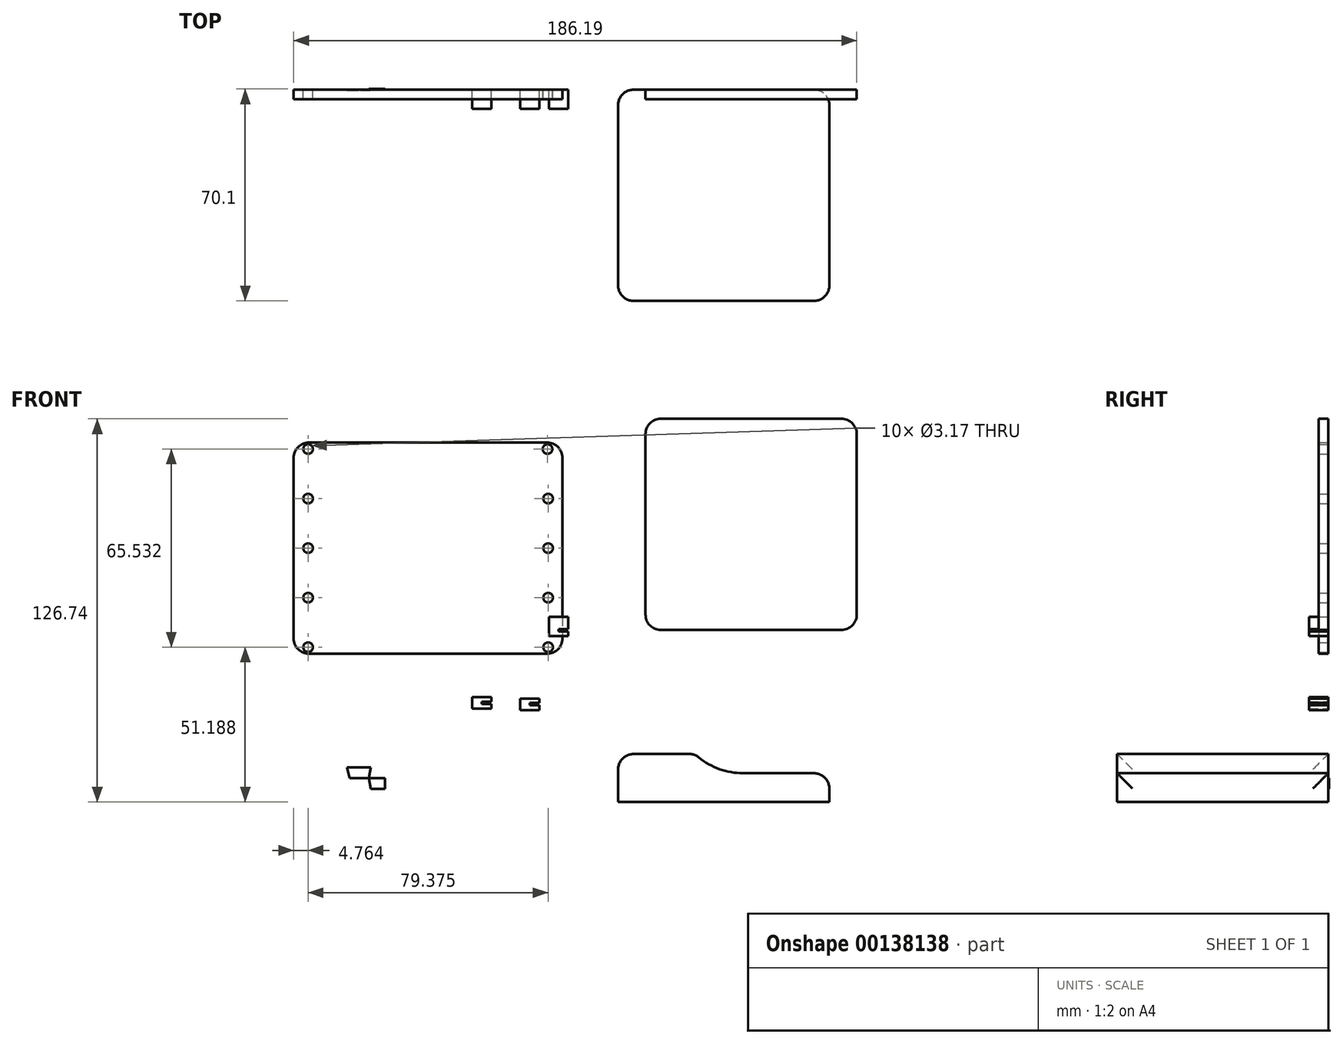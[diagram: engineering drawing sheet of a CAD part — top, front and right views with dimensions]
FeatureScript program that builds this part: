
annotation { "Feature Type Name" : "Feature", "Feature Type Description" : "" }
export const myFeature = defineFeature(function(context is Context, id is Id, definition is map)
    precondition{}
    {
        {
            var Q0;
            Q0=qCreatedBy(makeId("Front.planeOp"),FACE);
            var sketch = newSketch(context, id + "F0", { "sketchPlane" : qUnion([Q0])});
            skLineSegment(sketch, "E0.bottom", {"start": v(-88.22, 61.99) * mm, "end": v(0.68, 61.99) * mm});
            skLineSegment(sketch, "E0.top", {"start": v(-88.22, -7.86) * mm, "end": v(0.68, -7.86) * mm});
            skLineSegment(sketch, "E0.left", {"start": v(-88.22, 61.99) * mm, "end": v(-88.22, -7.86) * mm});
            skLineSegment(sketch, "E0.right", {"start": v(0.68, 61.99) * mm, "end": v(0.68, -7.86) * mm});
            skLineSegment(sketch, "E1", {"start": v(-78.7, 61.99) * mm, "end": v(-78.7, -7.86) * mm});
            skLineSegment(sketch, "E2", {"start": v(-8.84, 61.99) * mm, "end": v(-8.84, -7.86) * mm});
            skPoint(sketch, "E3.end.orphan", {"position": v(-78.7, 41.86) * mm});
            skPoint(sketch, "E4.end.orphan", {"position": v(-8.84, 36.83) * mm});
            skPoint(sketch, "E4.start.orphan", {"position": v(0.68, 41.86) * mm});
            skCircle(sketch, "E5", {"center": v(-83.46, 27.06) * mm, "radius": 1.59 * mm});
            skPoint(sketch, "E6.orphan", {"position": v(-88.22, 27.06) * mm});
            skPoint(sketch, "E7.trimOffspring.end.orphan", {"position": v(-78.7, 27.06) * mm});
            skCircle(sketch, "E8", {"center": v(-83.46, -5.7) * mm, "radius": 1.59 * mm});
            skPoint(sketch, "E9.end.orphan", {"position": v(-83.46, -7.29) * mm});
            skCircle(sketch, "E10", {"center": v(-83.46, 10.68) * mm, "radius": 1.59 * mm});
            skPoint(sketch, "E11.end.orphan", {"position": v(-83.46, -4.11) * mm});
            skPoint(sketch, "E11.start.orphan", {"position": v(-83.46, 9.1) * mm});
            skPoint(sketch, "E12.end.orphan", {"position": v(-83.46, 12.27) * mm});
            skPoint(sketch, "E12.start.orphan", {"position": v(-83.46, 25.48) * mm});
            skCircle(sketch, "E13", {"center": v(-83.46, 59.83) * mm, "radius": 1.59 * mm});
            skCircle(sketch, "E14", {"center": v(-83.46, 43.45) * mm, "radius": 1.59 * mm});
            skPoint(sketch, "E15.orphan", {"position": v(-83.46, 61.42) * mm});
            skPoint(sketch, "E16.end.orphan", {"position": v(-83.46, 58.24) * mm});
            skPoint(sketch, "E17.orphan", {"position": v(-83.46, 45.03) * mm});
            skPoint(sketch, "E18.end.orphan", {"position": v(-83.46, 41.86) * mm});
            skPoint(sketch, "E18.start.orphan", {"position": v(-83.46, 28.65) * mm});
            skCircle(sketch, "E19", {"center": v(-4.08, 27.06) * mm, "radius": 1.59 * mm});
            skCircle(sketch, "E20", {"center": v(-4.08, 10.68) * mm, "radius": 1.59 * mm});
            skCircle(sketch, "E21", {"center": v(-4.08, -5.7) * mm, "radius": 1.59 * mm});
            skPoint(sketch, "E22.end.orphan", {"position": v(-4.08, -7.29) * mm});
            skPoint(sketch, "E23.end.orphan", {"position": v(-4.08, -4.11) * mm});
            skPoint(sketch, "E23.start.orphan", {"position": v(-4.08, 9.1) * mm});
            skPoint(sketch, "E24.start.orphan", {"position": v(-4.08, 12.27) * mm});
            skPoint(sketch, "E25.orphan", {"position": v(-8.84, 27.06) * mm});
            skPoint(sketch, "E26.orphan", {"position": v(0.68, 27.06) * mm});
            skCircle(sketch, "E27", {"center": v(-4.08, 43.45) * mm, "radius": 1.59 * mm});
            skCircle(sketch, "E28", {"center": v(-4.28, 59.83) * mm, "radius": 1.59 * mm});
            skPoint(sketch, "E29.orphan", {"position": v(-4.28, 61.42) * mm});
            skPoint(sketch, "E30.end.orphan", {"position": v(-4.28, 58.24) * mm});
            skPoint(sketch, "E31.orphan", {"position": v(-4.08, 45.03) * mm});
            skPoint(sketch, "E32.end.orphan", {"position": v(-4.08, 41.86) * mm});
            skPoint(sketch, "E32.start.orphan", {"position": v(-4.08, 28.65) * mm});
            skSolve(sketch);
        }
        {
            var Q0;
            Q0 = qSketchRegion(id + "F0", true);
            extrude(context, id + "F1", {"entities" : qUnion([Q0]), "depth" : 3.17 * mm});
        }
        {
            var Q0;
            Q0=makeQuery(id+"F1.opExtrude","SWEPT_EDGE",EDGE,{"disambiguationData":[OSD([sQuery(id+"F0.wireOp",EDGE,"E0.top"),sQuery(id+"F0.wireOp",EDGE,"E0.left")])]});
            var Q1;
            Q1=makeQuery(id+"F1.opExtrude","SWEPT_EDGE",EDGE,{"disambiguationData":[OSD([sQuery(id+"F0.wireOp",EDGE,"E0.top"),sQuery(id+"F0.wireOp",EDGE,"E0.right")])]});
            var Q2;
            Q2=makeQuery(id+"F1.opExtrude","SWEPT_EDGE",EDGE,{"disambiguationData":[OSD([sQuery(id+"F0.wireOp",EDGE,"E0.bottom"),sQuery(id+"F0.wireOp",EDGE,"E0.right")])]});
            var Q3;
            Q3=makeQuery(id+"F1.opExtrude","SWEPT_EDGE",EDGE,{"disambiguationData":[OSD([sQuery(id+"F0.wireOp",EDGE,"E0.bottom"),sQuery(id+"F0.wireOp",EDGE,"E0.left")])]});
            fillet(context, id + "F2", {"entities" : qUnion([Q0, Q1, Q2, Q3]), "radius" : 5.08 * mm, "tangentPropagation" : true, "allowEdgeOverflow" : false});
        }
        {
            var Q0;
            Q0=qCreatedBy(makeId("Front.planeOp"),FACE);
            var sketch = newSketch(context, id + "F3", { "sketchPlane" : qUnion([Q0])});
            skLineSegment(sketch, "E33.bottom", {"start": v(28.12, 69.85) * mm, "end": v(97.97, 69.85) * mm});
            skLineSegment(sketch, "E33.top", {"start": v(28.12, 0) * mm, "end": v(97.97, 0) * mm});
            skLineSegment(sketch, "E33.left", {"start": v(28.12, 69.85) * mm, "end": v(28.12, 0) * mm});
            skLineSegment(sketch, "E33.right", {"start": v(97.97, 69.85) * mm, "end": v(97.97, 0) * mm});
            skSolve(sketch);
        }
        {
            var Q0;
            Q0 = qSketchRegion(id + "F3", true);
            extrude(context, id + "F4", {"entities" : qUnion([Q0]), "depth" : 3.17 * mm});
        }
        {
            var Q0;
            Q0=makeQuery(id+"F4.opExtrude","SWEPT_EDGE",EDGE,{"disambiguationData":[OSD([sQuery(id+"F3.wireOp",EDGE,"E33.bottom"),sQuery(id+"F3.wireOp",EDGE,"E33.left")])]});
            var Q1;
            Q1=makeQuery(id+"F4.opExtrude","SWEPT_EDGE",EDGE,{"disambiguationData":[OSD([sQuery(id+"F3.wireOp",EDGE,"E33.top"),sQuery(id+"F3.wireOp",EDGE,"E33.left")])]});
            var Q2;
            Q2=makeQuery(id+"F4.opExtrude","SWEPT_EDGE",EDGE,{"disambiguationData":[OSD([sQuery(id+"F3.wireOp",EDGE,"E33.top"),sQuery(id+"F3.wireOp",EDGE,"E33.right")])]});
            var Q3;
            Q3=makeQuery(id+"F4.opExtrude","SWEPT_EDGE",EDGE,{"disambiguationData":[OSD([sQuery(id+"F3.wireOp",EDGE,"E33.bottom"),sQuery(id+"F3.wireOp",EDGE,"E33.right")])]});
            fillet(context, id + "F5", {"entities" : qUnion([Q0, Q1, Q2, Q3]), "radius" : 5.08 * mm, "tangentPropagation" : true, "allowEdgeOverflow" : false});
        }
        {
            var Q0;
            Q0=qCreatedBy(makeId("Front.planeOp"),FACE);
            var sketch = newSketch(context, id + "F6", { "sketchPlane" : qUnion([Q0])});
            skLineSegment(sketch, "E34", {"start": v(19.06, -56.9) * mm, "end": v(88.9, -56.9) * mm});
            skLineSegment(sketch, "E35", {"start": v(19.06, -56.9) * mm, "end": v(19.06, -41.02) * mm});
            skLineSegment(sketch, "E36", {"start": v(19.06, -41.02) * mm, "end": v(44.46, -41.02) * mm});
            skLineSegment(sketch, "E37", {"start": v(88.9, -56.9) * mm, "end": v(88.9, -47.37) * mm});
            skLineSegment(sketch, "E38", {"start": v(88.9, -47.37) * mm, "end": v(60.33, -47.37) * mm});
            skArc(sketch, "E39", {"start": v(44.46, -41.02) * mm, "mid": v(51.78, -45.72) * mm, "end": v(60.33, -47.37) * mm});
            skPoint(sketch, "E40.start.orphan", {"position": v(44.46, -47.37) * mm});
            skSolve(sketch);
        }
        {
            var Q0;
            Q0 = qSketchRegion(id + "F6", true);
            extrude(context, id + "F7", {"entities" : qUnion([Q0]), "depth" : 69.85 * mm});
        }
        {
            var Q0;
            Q0=makeQuery(id+"F7.opExtrude","SWEPT_EDGE",EDGE,{"disambiguationData":[OSD([sQuery(id+"F6.wireOp",EDGE,"E35"),sQuery(id+"F6.wireOp",EDGE,"E36")])]});
            var Q1;
            Q1=makeQuery(id+"F7.opExtrude","SWEPT_EDGE",EDGE,{"disambiguationData":[OSD([sQuery(id+"F6.wireOp",EDGE,"E36"),sQuery(id+"F6.wireOp",EDGE,"E39")])]});
            var Q2;
            Q2=makeQuery(id+"F7.opExtrude","SWEPT_EDGE",EDGE,{"disambiguationData":[OSD([sQuery(id+"F6.wireOp",EDGE,"E37"),sQuery(id+"F6.wireOp",EDGE,"E38")])]});
            var Q3;
            Q3=makeQuery(id+"F7.opExtrude","CAP_EDGE",EDGE,{"disambiguationData":[OSD([sQuery(id+"F6.wireOp",EDGE,"E37")])],"isStart":true});
            var Q4;
            Q4=makeQuery(id+"F7.opExtrude","CAP_EDGE",EDGE,{"disambiguationData":[OSD([sQuery(id+"F6.wireOp",EDGE,"E35")])],"isStart":true});
            var Q5;
            Q5=makeQuery(id+"F7.opExtrude","CAP_EDGE",EDGE,{"disambiguationData":[OSD([sQuery(id+"F6.wireOp",EDGE,"E35")])],"isStart":false});
            var Q6;
            Q6=makeQuery(id+"F7.opExtrude","CAP_EDGE",EDGE,{"disambiguationData":[OSD([sQuery(id+"F6.wireOp",EDGE,"E37")])],"isStart":false});
            fillet(context, id + "F8", {"entities" : qUnion([Q0, Q1, Q2, Q3, Q4, Q5, Q6]), "radius" : 5.08 * mm, "tangentPropagation" : true, "allowEdgeOverflow" : false});
        }
        {
            var Q0;
            Q0=qCreatedBy(makeId("Front.planeOp"),FACE);
            var sketch = newSketch(context, id + "F9", { "sketchPlane" : qUnion([Q0])});
            skLineSegment(sketch, "E41", {"start": v(-69.73, -48.95) * mm, "end": v(-63.38, -48.95) * mm});
            skLineSegment(sketch, "E42", {"start": v(-70.59, -45.4) * mm, "end": v(-62.71, -45.4) * mm});
            skLineSegment(sketch, "E43", {"start": v(-70.59, -45.4) * mm, "end": v(-69.73, -48.95) * mm});
            skLineSegment(sketch, "E44", {"start": v(-62.71, -45.4) * mm, "end": v(-63.38, -48.95) * mm});
            skPoint(sketch, "E45.start.orphan", {"position": v(-66.65, -45.4) * mm});
            skSolve(sketch);
        }
        {
            var Q0;
            Q0 = qSketchRegion(id + "F9", true);
            extrude(context, id + "F10", {"entities" : qUnion([Q0]), "depth" : 0.25 * mm});
        }
        {
            var Q0;
            Q0=qCreatedBy(makeId("Front.planeOp"),FACE);
            var sketch = newSketch(context, id + "F11", { "sketchPlane" : qUnion([Q0])});
            skLineSegment(sketch, "E46", {"start": v(-63.38, -48.94) * mm, "end": v(-58.02, -48.94) * mm});
            skLineSegment(sketch, "E47", {"start": v(-63.38, -48.94) * mm, "end": v(-62.72, -52.52) * mm});
            skLineSegment(sketch, "E48", {"start": v(-62.72, -52.52) * mm, "end": v(-58.02, -52.52) * mm});
            skLineSegment(sketch, "E49", {"start": v(-58.02, -52.52) * mm, "end": v(-58.02, -48.94) * mm});
            skPoint(sketch, "E50.end.orphan", {"position": v(-62.72, -45.38) * mm});
            skPoint(sketch, "E51.end.orphan", {"position": v(-58.02, -45.38) * mm});
            skSolve(sketch);
        }
        {
            var Q0;
            Q0 = qSketchRegion(id + "F11", true);
            extrude(context, id + "F12", {"entities" : qUnion([Q0]), "operationType" : NewBodyOperationType.ADD, "oppositeDirection" : true, "depth" : 0.25 * mm});
        }
        {
            var Q0;
            Q0=qCreatedBy(makeId("Front.planeOp"),FACE);
            var sketch = newSketch(context, id + "F13", { "sketchPlane" : qUnion([Q0])});
            skLineSegment(sketch, "E52.bottom", {"start": v(-29.15, -22.21) * mm, "end": v(-22.8, -22.21) * mm});
            skLineSegment(sketch, "E52.top", {"start": v(-29.15, -26.02) * mm, "end": v(-22.8, -26.02) * mm});
            skLineSegment(sketch, "E52.left", {"start": v(-29.15, -22.21) * mm, "end": v(-29.15, -26.02) * mm});
            skPoint(sketch, "E53.endSnap0", {"position": v(-25.97, -22.21) * mm});
            skPoint(sketch, "E54.end.orphan", {"position": v(-25.97, -26.02) * mm});
            skPoint(sketch, "E55.orphan", {"position": v(-25.97, -30.47) * mm});
            skLineSegment(sketch, "E56", {"start": v(-22.8, -22.21) * mm, "end": v(-22.8, -23.7) * mm});
            skLineSegment(sketch, "E57", {"start": v(-22.8, -23.7) * mm, "end": v(-25.97, -23.7) * mm});
            skLineSegment(sketch, "E58", {"start": v(-25.97, -23.7) * mm, "end": v(-25.97, -24.45) * mm});
            skLineSegment(sketch, "E59", {"start": v(-25.97, -24.45) * mm, "end": v(-22.8, -24.45) * mm});
            skLineSegment(sketch, "E60", {"start": v(-22.8, -24.45) * mm, "end": v(-22.8, -26.02) * mm});
            skLineSegment(sketch, "E61.bottom", {"start": v(-3.75, 4.31) * mm, "end": v(2.6, 4.31) * mm});
            skLineSegment(sketch, "E61.top", {"start": v(-3.75, -2.04) * mm, "end": v(2.6, -2.04) * mm});
            skLineSegment(sketch, "E61.left", {"start": v(-3.75, 4.31) * mm, "end": v(-3.75, -2.04) * mm});
            skPoint(sketch, "E62.endSnap0", {"position": v(-0.58, 4.31) * mm});
            skPoint(sketch, "E63.end.orphan", {"position": v(-0.58, -2.04) * mm});
            skPoint(sketch, "E64.orphan", {"position": v(-0.58, -6.48) * mm});
            skLineSegment(sketch, "E65", {"start": v(2.6, 4.31) * mm, "end": v(2.6, 0.3) * mm});
            skLineSegment(sketch, "E66", {"start": v(2.6, 0.3) * mm, "end": v(-0.58, 0.3) * mm});
            skLineSegment(sketch, "E67", {"start": v(-0.58, 0.3) * mm, "end": v(-0.58, -0.46) * mm});
            skLineSegment(sketch, "E68", {"start": v(-0.58, -0.46) * mm, "end": v(2.6, -0.46) * mm});
            skLineSegment(sketch, "E69", {"start": v(2.6, -0.46) * mm, "end": v(2.6, -2.04) * mm});
            skSolve(sketch);
        }
        {
            var Q0;
            Q0 = qSketchRegion(id + "F13", true);
            extrude(context, id + "F14", {"entities" : qUnion([Q0]), "depth" : 6.35 * mm});
        }
        {
            var Q0;
            Q0=qCreatedBy(makeId("Front.planeOp"),FACE);
            var sketch = newSketch(context, id + "F15", { "sketchPlane" : qUnion([Q0])});
            skLineSegment(sketch, "E70.bottom", {"start": v(-3.75, 4.31) * mm, "end": v(2.6, 4.31) * mm});
            skLineSegment(sketch, "E70.top", {"start": v(-3.75, -2.04) * mm, "end": v(2.6, -2.04) * mm});
            skLineSegment(sketch, "E70.left", {"start": v(-3.75, 4.31) * mm, "end": v(-3.75, -2.04) * mm});
            skPoint(sketch, "E71.endSnap0", {"position": v(-0.58, 4.31) * mm});
            skPoint(sketch, "E72.end.orphan", {"position": v(-0.58, -2.04) * mm});
            skPoint(sketch, "E73.orphan", {"position": v(-0.58, -6.48) * mm});
            skLineSegment(sketch, "E74", {"start": v(2.6, 4.31) * mm, "end": v(2.6, 0.3) * mm});
            skLineSegment(sketch, "E75", {"start": v(2.6, 0.3) * mm, "end": v(-0.58, 0.3) * mm});
            skLineSegment(sketch, "E76", {"start": v(-0.58, 0.3) * mm, "end": v(-0.58, -0.46) * mm});
            skLineSegment(sketch, "E77", {"start": v(-0.58, -0.46) * mm, "end": v(2.6, -0.46) * mm});
            skLineSegment(sketch, "E78", {"start": v(2.6, -0.46) * mm, "end": v(2.6, -2.04) * mm});
            skLineSegment(sketch, "E79.bottom", {"start": v(-13.29, -22.68) * mm, "end": v(-6.94, -22.68) * mm});
            skLineSegment(sketch, "E79.top", {"start": v(-13.29, -26.49) * mm, "end": v(-6.94, -26.49) * mm});
            skLineSegment(sketch, "E79.left", {"start": v(-13.29, -22.68) * mm, "end": v(-13.29, -26.49) * mm});
            skPoint(sketch, "E80.endSnap0", {"position": v(-10.11, -22.68) * mm});
            skPoint(sketch, "E81.end.orphan", {"position": v(-10.11, -26.49) * mm});
            skPoint(sketch, "E82.orphan", {"position": v(-10.11, -30.93) * mm});
            skLineSegment(sketch, "E83", {"start": v(-6.94, -22.68) * mm, "end": v(-6.94, -24.16) * mm});
            skLineSegment(sketch, "E84", {"start": v(-6.94, -24.16) * mm, "end": v(-10.11, -24.16) * mm});
            skLineSegment(sketch, "E85", {"start": v(-10.11, -24.16) * mm, "end": v(-10.11, -24.92) * mm});
            skLineSegment(sketch, "E86", {"start": v(-10.11, -24.92) * mm, "end": v(-6.94, -24.92) * mm});
            skLineSegment(sketch, "E87", {"start": v(-6.94, -24.92) * mm, "end": v(-6.94, -26.49) * mm});
            skSolve(sketch);
        }
        {
            var Q0;
            Q0 = qSketchRegion(id + "F15", true);
            extrude(context, id + "F16", {"entities" : qUnion([Q0]), "depth" : 6.35 * mm});
        }
    });
